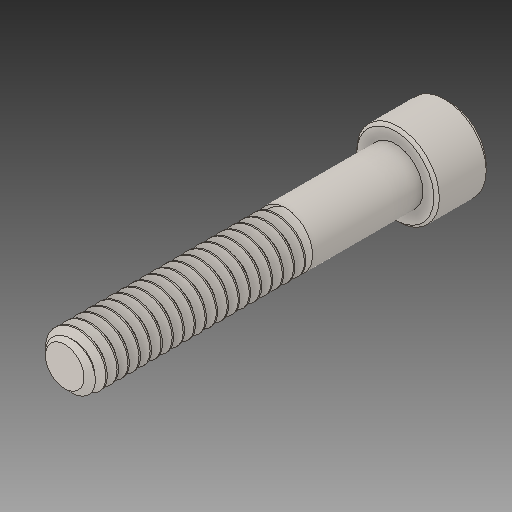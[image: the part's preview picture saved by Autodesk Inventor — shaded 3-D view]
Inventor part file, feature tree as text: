
AUTODESK INVENTOR PART (.ipt)
format: ipt  version: 2017 (Build 210142000, 142)  size: 722,432 bytes
history: native  units: in
note: dims shown in document units (in); Inventor stores cm internally (conversion verified against a paired STEP export)
features: chamfer x1
ambient origin geometry x8: Origin, YZ Plane, XZ Plane, XY Plane, X Axis, Y Axis, Z Axis, Center Point
bodies: Solid1 (feature_tree)
feature tree (1):
  chamfer  "Chamfer2"  [1 undecoded]
note: 1 required parameter value undecoded (feature->parameter linkage not recoverable at this tier; creation-order binding heuristic only, values carry confidence <= 0.55)
